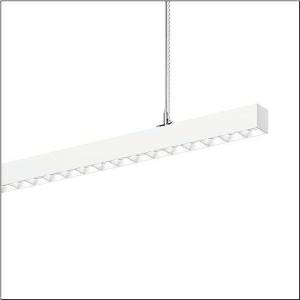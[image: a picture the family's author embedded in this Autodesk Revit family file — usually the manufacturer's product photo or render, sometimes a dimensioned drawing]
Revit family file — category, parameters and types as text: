
# Revit family: silica_r__21_51mx37da47wb_26de
name_source: partatom
category: Lighting Fixtures
units: mm (PartAtom-declared; Revit-internal decimal feet)

## family parameters
Cut with Voids When Loaded = No
Host = Face
Light Source = No
Part Type = Normal
Room Calculation Point = No
Round Connector Dimension = Use Diameter
Shared = No

## types (1)
- --- (1 x LED, 7300 lm, 44 W, 4000K)
    Apparent Load = 44 VA
    CIE Flux Codes = 71 92 99 59 100
    Color Rendering = 80
    Color Temperature = 4000K
    Default Elevation = 1800 mm
    Description = Silica® 21, office luminaire, primary light control with darklight reflector, of PMMA, white, CAT 2 (L<= 3000cd/m²), light emission: direct/indirect distribution, primary light characteristic: asymmetric, installation type: suspended mounting, LED, rated luminous flux: 7.300lm, luminous efficacy: 166lm/W, light colour: 840, colour temperature: 4000K, with terminal, 3+2-pole, max. 2.5mm², mains connection: 220..240V, AC, 50/60Hz, rated input power: 44W, luminaire housing, of aluminium, traffic white (RAL 9016), length: 1.204mm, width: 53mm, height: 53mm, protection rating (complete): IP20, insulation class (complete): insulation class I (protective earthing), certification: CE, permissible operating ambient temperature: 0..+35°C, standard: EN 50419, packaging unit: 1 piece
    Height = 53 mm
    Lamp = 1 x LED
    Lamp Light Flux = 7300 lm
    Lamp Power = 44 W
    Lamp count = 1
    Length = 1204 mm
    Luminous efficacy = 166 lm/W
    Manufacturer = Siteco
    ModVariant = No
    Model = 51MX37DA47WB
    Mounting Place = Ceiling
    Mounting Type = Pendant
    Number of Poles = 1
    OnlyDefault = Yes
    Power Factor = 1
    Product Name = Silica® 21
    Product group = office luminaire | ceiling pendant
    ProductGroupID = 905
    Protection Class = Protection class I
    Protection Degree = IP 20
    RLX_Detail_Level = 1
    RlxData = <blob elided: 41709 chars, md5=51ef27cd>
    Socket = socket
    Standby Power = 0 W
    System Light Flux = 7300 lm
    System Power = 44 W
    Type Comments = factory setting: luminous flux: 100 % | dim-lin: 254 | 368 mA
    Type Image = l_1251641.jpg
    URL = http://relux.com
    VarID = @adj_028733
    Voltage = 0 V
    Weight = 0.00 kg
    Width = 53 mm

## geometry (parser evidence)
native form markers: Blend x4, Sweep x11
no freeform markers — native parametric forms only
